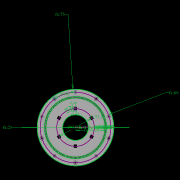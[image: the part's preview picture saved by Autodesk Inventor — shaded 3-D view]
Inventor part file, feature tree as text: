
AUTODESK INVENTOR PART (.ipt)
format: ipt  version: 2022.2 (Build 262287010, 287A)  size: 1,486,336 bytes
history: native  units: mm
features: extrude x26, other x19, sketch x16, pattern_circular x10, plane x4, fillet x2, move_body x2, revolve x2, draft x2, chamfer x2
ambient origin geometry x8: Origin, YZ Plane, XZ Plane, XY Plane, X Axis, Y Axis, Z Axis, Center Point
bodies: Solid5 (feature_tree)
feature tree (85):
  other  "CrossSection1"
  sketch  "Sketch7"  dims[d167=8.972256mm]
  other  "Roller1"
  other  "Roller2"
  sketch  "Sketch22"  dims[d173=10.814812mm]
  sketch  "Sketch2"  dims[d57=4.025mm d90=61.984365mm]
  sketch  "Sketch23"  dims[d201=75.0mm d232=0.0mm d233=3600.0mm]
  other  "RevRoller1"
  fillet  "Fillet1"  Radius=59.246882mm
  extrude  "Extrusion39"  Depth=61.984365mm
  pattern_circular  "Circular Pattern13"  Count=360  [1 undecoded]
  move_body  "Move Body7"
  revolve  "Revolution13"  [1 undecoded]
  fillet  "Fillet3"  Radius=0.025mm
  pattern_circular  "Circular Pattern14"  [2 undecoded]
  move_body  "Move Body6"
  revolve  "Revolution14"  [1 undecoded]
  other  "OuterRim_Top2"
  other  "OuterRim_Bottom2"
  plane  "Work Plane8"
  sketch  "Sketch49"  dims[d352=0.025mm]
  sketch  "Sketch50"  dims[d354=0.025mm]
  sketch  "Sketch51"  dims[d355=16.1595mm]
  extrude  "Extrusion40"  TaperAngle=360.0deg  [1 undecoded]
  extrude  "Extrusion41"  Depth=0.5mm
  extrude  "Extrusion42"  Depth=0.5mm
  extrude  "Extrusion43"  Depth=0.5mm
  sketch  "Sketch52"  dims[d356=16.159664mm]
  extrude  "Extrusion44"  Depth=1.0mm
  extrude  "Extrusion45"  Depth=0.5mm
  extrude  "Extrusion46"  TaperAngle=90.0deg  [1 undecoded]
  extrude  "Extrusion47"  Depth=0.5mm
  pattern_circular  "Circular Pattern32"  Count=24  [1 undecoded]
  pattern_circular  "Circular Pattern33"  Angle=360.0deg  [1 undecoded]
  sketch  "Sketch57"  dims[d358=360.0deg d359=0.5mm d360=240.0mm d361=360.0deg d363=1.308997mm d367=8.1mm d370=0.025mm d371=1.0mm d372=1.308997mm d373=90.0deg d374=0.5mm d375=240.0mm d376=360.0deg d378=90.0deg d379=0.1mm d380=0.025mm d381=0.025mm d382=0.025mm d383=0.025mm d384=11.193516mm d385=0.0mm d386=0.0mm d391=25.0mm d392=75.0mm d393=1.5mm d394=1.5mm d395=1.5mm d396=1.5mm d397=90.0deg d398=90.0deg d399=90.0deg d400=75.0mm d401=11.193516mm d402=0.0mm d486=0.436332mm d487=0.5mm d488=2.0mm d489=0.0mm d490=20.0mm d495=2.5mm d496=8.0mm d506=13.856406mm d507=55.5mm d508=8.0mm d509=0.05mm d510=2.5mm d511=30.0deg d512=12.0mm d513=6.0mm d514=0.2mm d515=30.0deg d516=131.0mm d517=65.5mm d518=0.2mm d519=100.0mm d520=120.0mm d521=2.0mm d522=150.0mm d530=50.0mm d531=5.5mm d532=5.5mm d533=5.5mm d534=85.75mm d535=73.5mm d536=61.25mm d537=24.5mm d538=3.0mm d539=2.4mm d540=0.0mm d541=0.0mm d542=0.0mm d543=5.5mm d544=3.0mm d545=0.0mm d546=90.0mm d547=360.0deg d549=3.0mm d550=3.0mm d551=2.4mm d552=0.0mm d553=5.596758mm d554=0.0mm d555=2.4mm d556=0.0mm d557=5.596758mm d558=0.0mm d559=5.596758mm d560=0.0mm d561=90.0mm d562=360.0deg d564=60.0mm d565=360.0deg d567=5.5mm d568=5.5mm d569=3.0mm d570=0.0mm d571=5.596758mm d572=0.0mm d573=3.0mm d574=0.0mm d575=5.596758mm d576=0.0mm d577=90.0mm d578=360.0deg d580=60.0mm d581=360.0deg d584=20.0mm d585=8.0mm d587=1.75mm d589=3.0mm d592=2.0mm d593=12.0mm d594=12.0mm d600=0.5mm d601=2.0mm d602=45.0deg d603=0.5mm d604=2.0mm d605=45.0deg d606=0.436332mm d607=0.5mm d608=0.0mm d609=20.0mm d611=360.0deg d613=0.0mm d614=0.0mm d617=0.99971mm d618=100.0mm d620=69.0mm d621=5.0mm d622=0.5mm d623=0.5mm d624=5.0mm d625=0.2mm d626=0.0mm d627=20.0mm d629=69.0mm d630=73.5mm d631=20.0mm d633=6.283185mm d635=5.5mm d636=3.0mm d637=7.0mm d638=4.0mm d639=5.596758mm d640=0.0mm d641=3.0mm d642=0.0mm d643=5.596758mm d644=0.0mm d645=4.0mm d646=0.0mm d647=20.0mm d649=6.283185mm d651=3.0mm d652=4.0mm d653=20.0mm d655=6.283185mm d657=7.0mm d658=5.5mm d659=5.596758mm d660=0.0mm d661=2.593516mm d662=0.0mm d663=5.596758mm d664=0.0mm d665=3.193516mm d666=0.0mm d679=50.0mm d680=360.0deg d682=50.0mm d683=360.0deg d694=6.35mm d695=6.35mm d696=6.4mm d697=5.45mm d698=11.194mm d699=0.0mm d700=8.194mm d701=0.0mm d702=60.0mm d703=360.0deg d16=0.872665mm d17=0.872665mm d49=0.872665mm d50=0.872665mm d51=0.872665mm d52=0.872665mm d236=0.5mm d237=0.872665mm d238=0.5mm d239=0.872665mm d282=1.0mm d283=1.0mm d284=1.0mm d285=0.15mm d286=0.25mm d287=0.375mm d288=14.3117mm d289=0.75mm d290=20.594885mm d291=0.0625mm d292=0.75mm d293=0.375mm d405=0.5mm d406=0.872665mm d407=0.5mm d408=0.872665mm d413=0.5mm d414=0.872665mm d415=0.5mm d416=0.872665mm d417=0.5mm d418=0.872665mm d419=0.5mm d420=0.872665mm d421=0.872665mm d431=0.5mm d432=0.872665mm d433=0.5mm d434=0.872665mm d471=0.5mm d472=0.872665mm d473=0.5mm d474=0.872665mm d497=0.5mm d498=0.872665mm d499=0.5mm d500=0.872665mm d590=0.5mm d591=0.872665mm]
  extrude  "Extrusion50"  TaperAngle=90.0deg  [1 undecoded]
  extrude  "Extrusion51"  Depth=0.1mm
  pattern_circular  "Circular Pattern34"  [2 undecoded]
  plane  "Work Plane7"
  sketch  "Sketch47"  dims[d350=47.575427mm]
  extrude  "Rotor_Ring"  Depth=0.5mm
  draft  "FaceDraft2"
  sketch  "Sketch30"  dims[d343=16.1595mm d344=16.159664mm d345=0.025mm]
  plane  "Work Plane5"
  other  "Rotor Featurs"
  other  "RotorRim_Bottom"
  extrude  "Extrusion24"  Depth=0.5mm
  extrude  "Extrusion25"  Depth=0.5mm
  extrude  "Extrusion26"  Depth=11.193516mm
  pattern_circular  "Circular Pattern23"  [2 undecoded]
  sketch  "Sketch41"  dims[d347=0.1mm]
  extrude  "Extrusion27"  TaperAngle=0.0deg  [1 undecoded]
  extrude  "Extrusion28"  Depth=25.0mm
  pattern_circular  "Circular Pattern24"  [2 undecoded]
  extrude  "Extrusion29"  Depth=1.5mm
  extrude  "Extrusion30"  Depth=1.5mm
  extrude  "Extrusion31"  Depth=1.5mm
  pattern_circular  "Circular Pattern25"  [2 undecoded]
  sketch  "Sketch42"  dims[d348=0.1mm]
  extrude  "Extrusion32"  TaperAngle=90.0deg  [1 undecoded]
  extrude  "Extrusion33"  TaperAngle=90.0deg  [1 undecoded]
  extrude  "Extrusion34"  TaperAngle=90.0deg  [1 undecoded]
  extrude  "Extrusion35"  Depth=0.5mm
  pattern_circular  "Circular Pattern26"  [2 undecoded]
  pattern_circular  "Circular Pattern27"  [2 undecoded]
  chamfer  "Chamfer1"  Distance=0.436332mm
  chamfer  "Chamfer2"  Distance=0.5mm
  draft  "FaceDraft4"
  plane  "Work Plane6"
  sketch  "Sketch43"  dims[d349=47.575591mm]
  extrude  "Extrusion37"  Depth=0.5mm
  extrude  "Extrusion38"  Depth=8.0mm
  other  "2D Equation Curve1"
  sketch  "Sketch40"  dims[d346=0.025mm]
  other  "Work Axis6"
  other  "Work Axis7"
  other  "Work Axis8"
  other  "Work Axis9"
  other  "Work Axis10"
  other  "Work Point1"
  other  "Work Point2"
  other  "Work Point3"
  other  "Work Point4"
  other  "Work Point5"
  sketch  "Sketch48"  dims[d351=0.025mm]
note: 26 required parameter values undecoded (feature->parameter linkage not recoverable at this tier; creation-order binding heuristic only, values carry confidence <= 0.55)